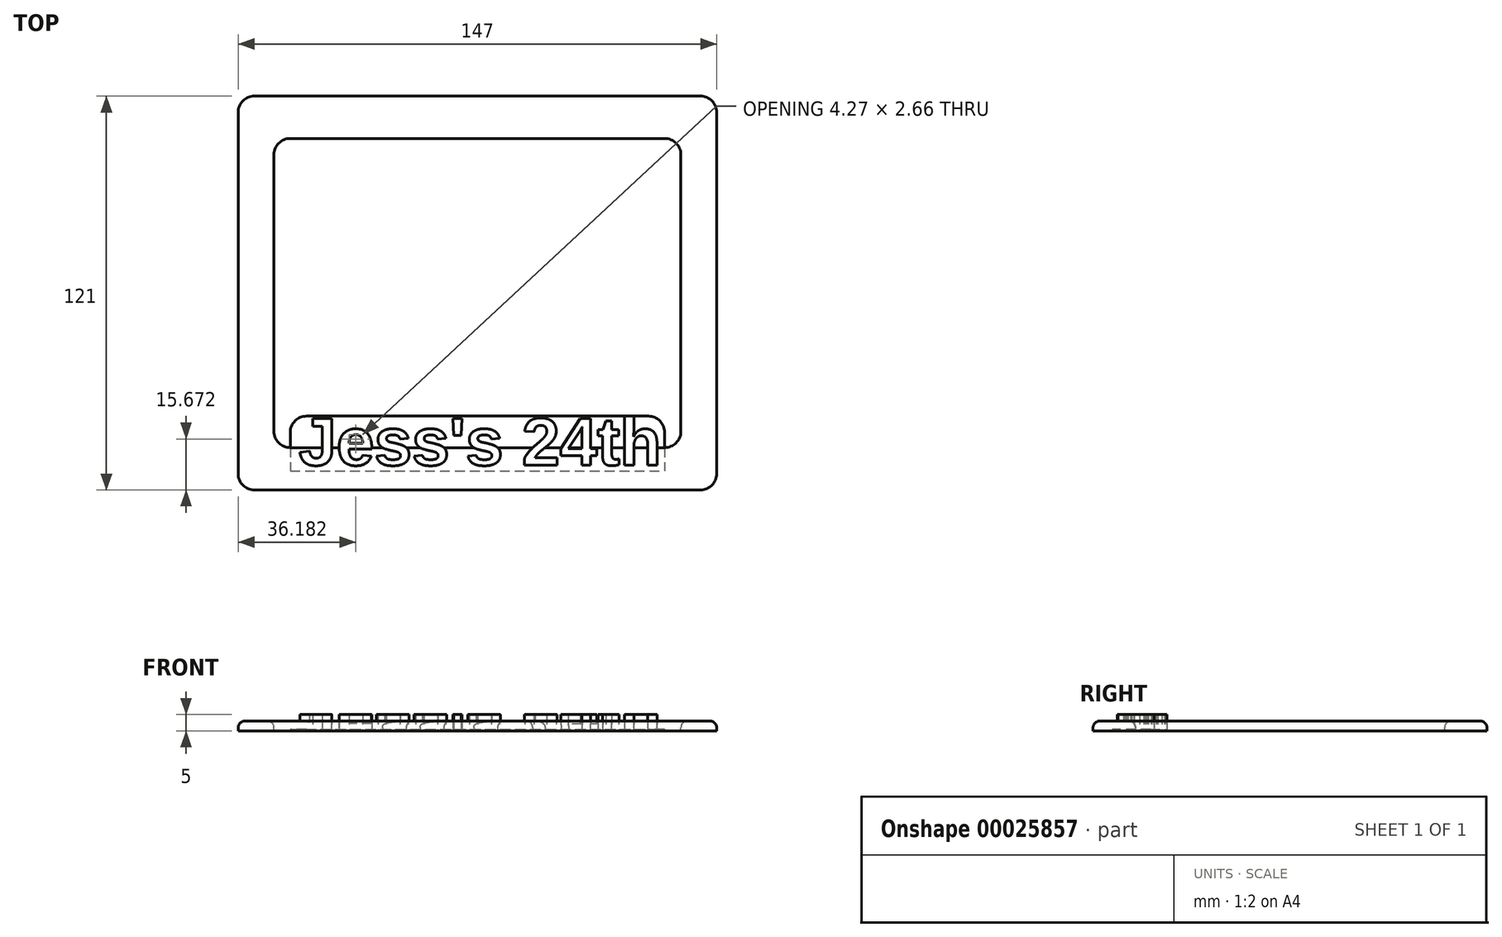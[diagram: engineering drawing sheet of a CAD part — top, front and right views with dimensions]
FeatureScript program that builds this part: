
annotation { "Feature Type Name" : "Feature", "Feature Type Description" : "" }
export const myFeature = defineFeature(function(context is Context, id is Id, definition is map)
    precondition{}
    {
        {
            var Q0;
            Q0=qCreatedBy(makeId("Top.planeOp"),FACE);
            var sketch = newSketch(context, id + "F0", { "sketchPlane" : qUnion([Q0])});
            skLineSegment(sketch, "E0.bottom", {"start": v(-73.5, 60.5) * mm, "end": v(73.5, 60.5) * mm});
            skLineSegment(sketch, "E0.top", {"start": v(-73.5, -60.5) * mm, "end": v(73.5, -60.5) * mm});
            skLineSegment(sketch, "E0.left", {"start": v(-73.5, 60.5) * mm, "end": v(-73.5, -60.5) * mm});
            skLineSegment(sketch, "E0.right", {"start": v(73.5, 60.5) * mm, "end": v(73.5, -60.5) * mm});
            skSolve(sketch);
        }
        {
            var Q0;
            Q0 = qSketchRegion(id + "F0", true);
            extrude(context, id + "F1", {"entities" : qUnion([Q0]), "depth" : 3 * mm});
        }
        {
            var Q0;
            Q0=makeQuery(id+"F1.opExtrude","SWEPT_EDGE",EDGE,{"disambiguationData":[OSD([sQuery(id+"F0.wireOp",EDGE,"E0.top"),sQuery(id+"F0.wireOp",EDGE,"E0.left")])]});
            var Q1;
            Q1=makeQuery(id+"F1.opExtrude","SWEPT_EDGE",EDGE,{"disambiguationData":[OSD([sQuery(id+"F0.wireOp",EDGE,"E0.top"),sQuery(id+"F0.wireOp",EDGE,"E0.right")])]});
            var Q2;
            Q2=makeQuery(id+"F1.opExtrude","SWEPT_EDGE",EDGE,{"disambiguationData":[OSD([sQuery(id+"F0.wireOp",EDGE,"E0.bottom"),sQuery(id+"F0.wireOp",EDGE,"E0.left")])]});
            var Q3;
            Q3=makeQuery(id+"F1.opExtrude","SWEPT_EDGE",EDGE,{"disambiguationData":[OSD([sQuery(id+"F0.wireOp",EDGE,"E0.bottom"),sQuery(id+"F0.wireOp",EDGE,"E0.right")])]});
            fillet(context, id + "F2", {"entities" : qUnion([Q0, Q1, Q2, Q3]), "radius" : 5 * mm, "tangentPropagation" : true, "allowEdgeOverflow" : false});
        }
        {
            var Q0;
            Q0=makeQuery(id+"F1.opExtrude","CAP_FACE",FACE,{"disambiguationData":[OSD([sQuery(id+"F0.wireOp",EDGE,"E0.bottom"),sQuery(id+"F0.wireOp",EDGE,"E0.top"),sQuery(id+"F0.wireOp",EDGE,"E0.left"),sQuery(id+"F0.wireOp",EDGE,"E0.right")])],"isStart":false});
            var sketch = newSketch(context, id + "F3", { "sketchPlane" : qUnion([Q0])});
            skLineSegment(sketch, "E1.bottom", {"start": v(-62.5, 47.5) * mm, "end": v(62.5, 47.5) * mm});
            skLineSegment(sketch, "E1.top", {"start": v(-62.5, -47.5) * mm, "end": v(62.5, -47.5) * mm});
            skLineSegment(sketch, "E1.left", {"start": v(-62.5, 47.5) * mm, "end": v(-62.5, -47.5) * mm});
            skLineSegment(sketch, "E1.right", {"start": v(62.5, 47.5) * mm, "end": v(62.5, -47.5) * mm});
            skSolve(sketch);
        }
        {
            var Q0;
            Q0 = qSketchRegion(id + "F3", true);
            var Q1;
            Q1=makeQuery(id+"F1.opExtrude","CAP_FACE",FACE,{"disambiguationData":[OSD([sQuery(id+"F0.wireOp",EDGE,"E0.bottom"),sQuery(id+"F0.wireOp",EDGE,"E0.top"),sQuery(id+"F0.wireOp",EDGE,"E0.left"),sQuery(id+"F0.wireOp",EDGE,"E0.right")])],"isStart":true});
            extrude(context, id + "F4", {"entities" : qUnion([Q0]), "operationType" : NewBodyOperationType.REMOVE, "endBound" : BoundingType.UP_TO_SURFACE, "oppositeDirection" : true, "endBoundEntityFace" : qUnion([Q1]), "depth" : 25 * mm});
        }
        {
            var Q0;
            Q0=makeQuery(id+"F4.boolean.opBoolean","COPY",EDGE,{"derivedFrom":makeQuery(id+"F4.opExtrude","SWEPT_EDGE",EDGE,{"disambiguationData":[OSD([sQuery(id+"F3.wireOp",EDGE,"E1.bottom"),sQuery(id+"F3.wireOp",EDGE,"E1.left")])]})});
            var Q1;
            Q1=makeQuery(id+"F4.boolean.opBoolean","COPY",EDGE,{"derivedFrom":makeQuery(id+"F4.opExtrude","SWEPT_EDGE",EDGE,{"disambiguationData":[OSD([sQuery(id+"F3.wireOp",EDGE,"E1.bottom"),sQuery(id+"F3.wireOp",EDGE,"E1.right")])]})});
            var Q2;
            Q2=makeQuery(id+"F4.boolean.opBoolean","COPY",EDGE,{"derivedFrom":makeQuery(id+"F4.opExtrude","SWEPT_EDGE",EDGE,{"disambiguationData":[OSD([sQuery(id+"F3.wireOp",EDGE,"E1.top"),sQuery(id+"F3.wireOp",EDGE,"E1.right")])]})});
            var Q3;
            Q3=makeQuery(id+"F4.boolean.opBoolean","COPY",EDGE,{"derivedFrom":makeQuery(id+"F4.opExtrude","SWEPT_EDGE",EDGE,{"disambiguationData":[OSD([sQuery(id+"F3.wireOp",EDGE,"E1.top"),sQuery(id+"F3.wireOp",EDGE,"E1.left")])]})});
            fillet(context, id + "F5", {"entities" : qUnion([Q0, Q1, Q2, Q3]), "radius" : 5 * mm, "tangentPropagation" : true, "allowEdgeOverflow" : false});
        }
        {
            var Q0;
            Q0=makeQuery(id+"F1.opExtrude","CAP_FACE",FACE,{"disambiguationData":[OSD([sQuery(id+"F0.wireOp",EDGE,"E0.bottom"),sQuery(id+"F0.wireOp",EDGE,"E0.top"),sQuery(id+"F0.wireOp",EDGE,"E0.left"),sQuery(id+"F0.wireOp",EDGE,"E0.right")])],"isStart":false});
            fillet(context, id + "F6", {"entities" : qUnion([Q0]), "radius" : 2 * mm, "tangentPropagation" : true, "allowEdgeOverflow" : false});
        }
        {
            var Q0;
            Q0=makeQuery(id+"F1.opExtrude","CAP_FACE",FACE,{"disambiguationData":[OSD([sQuery(id+"F0.wireOp",EDGE,"E0.bottom"),sQuery(id+"F0.wireOp",EDGE,"E0.top"),sQuery(id+"F0.wireOp",EDGE,"E0.left"),sQuery(id+"F0.wireOp",EDGE,"E0.right")])],"isStart":false});
            var sketch = newSketch(context, id + "F7", { "sketchPlane" : qUnion([Q0])});
            skText(sketch, "E2", { "text": "Jess\'s 24th", "fontName": "Arimo-Bold.ttf"});
            const initialGuessF7  = {"E2": [-0.05484, -0.05289, 1, 0, 0.01497]};
            skSetInitialGuess(sketch, initialGuessF7);
            skSolve(sketch);
        }
        {
            var Q0;
            Q0 = qSketchRegion(id + "F7", true);
            var Q1;
            Q1=makeQuery(id+"F1.opExtrude","CAP_FACE",FACE,{"disambiguationData":[OSD([sQuery(id+"F0.wireOp",EDGE,"E0.bottom"),sQuery(id+"F0.wireOp",EDGE,"E0.top"),sQuery(id+"F0.wireOp",EDGE,"E0.left"),sQuery(id+"F0.wireOp",EDGE,"E0.right")])],"isStart":true});
            extrude(context, id + "F8", {"entities" : qUnion([Q0]), "operationType" : NewBodyOperationType.ADD, "depth" : 2 * mm, "hasSecondDirection" : true, "secondDirectionBound" : SecondDirectionBoundingType.UP_TO_SURFACE, "secondDirectionOppositeDirection" : true, "secondDirectionBoundEntityFace" : qUnion([Q1]), "secondDirectionDepth" : 25 * mm});
        }
        {
            var Q0;
            Q0=qCreatedBy(makeId("Top.planeOp"),FACE);
            var sketch = newSketch(context, id + "F9", { "sketchPlane" : qUnion([Q0])});
            skLineSegment(sketch, "E3.bottom", {"start": v(-57.5, -37.82) * mm, "end": v(57.5, -37.82) * mm});
            skLineSegment(sketch, "E3.top", {"start": v(-57.5, -54.6) * mm, "end": v(57.5, -54.6) * mm});
            skLineSegment(sketch, "E3.left", {"start": v(-57.5, -37.82) * mm, "end": v(-57.5, -54.6) * mm});
            skLineSegment(sketch, "E3.right", {"start": v(57.5, -37.82) * mm, "end": v(57.5, -54.6) * mm});
            skSolve(sketch);
        }
        {
            var Q0;
            Q0 = qSketchRegion(id + "F9", true);
            extrude(context, id + "F10", {"entities" : qUnion([Q0]), "depth" : 0.5 * mm});
        }
        {
            var Q0;
            Q0=makeQuery(id+"F10.opExtrude","SWEPT_EDGE",EDGE,{"disambiguationData":[OSD([sQuery(id+"F9.wireOp",EDGE,"E3.bottom"),sQuery(id+"F9.wireOp",EDGE,"E3.left")])]});
            fillet(context, id + "F11", {"entities" : qUnion([Q0]), "radius" : 5 * mm, "tangentPropagation" : true, "allowEdgeOverflow" : false});
        }
        {
            var Q0;
            Q0=makeQuery(id+"F10.opExtrude","SWEPT_EDGE",EDGE,{"disambiguationData":[OSD([sQuery(id+"F9.wireOp",EDGE,"E3.bottom"),sQuery(id+"F9.wireOp",EDGE,"E3.right")])]});
            fillet(context, id + "F12", {"entities" : qUnion([Q0]), "radius" : 5 * mm, "tangentPropagation" : true, "allowEdgeOverflow" : false});
        }
    });
